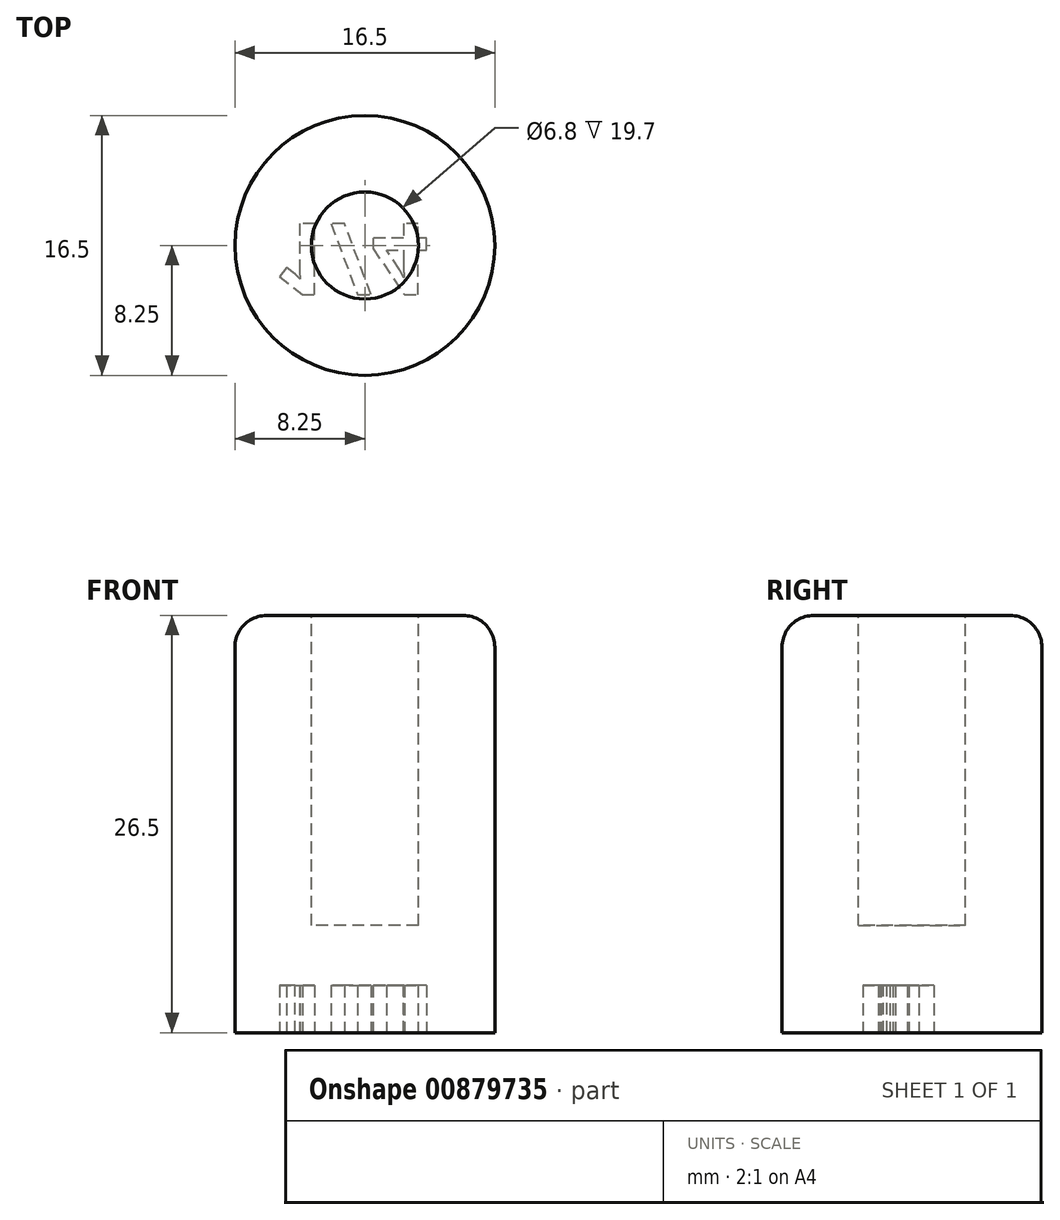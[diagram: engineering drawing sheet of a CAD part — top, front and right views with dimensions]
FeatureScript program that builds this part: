
annotation { "Feature Type Name" : "Feature", "Feature Type Description" : "" }
export const myFeature = defineFeature(function(context is Context, id is Id, definition is map)
    precondition{}
    {
        {
            var Q0;
            Q0=qCreatedBy(makeId("Top.planeOp"),FACE);
            var sketch = newSketch(context, id + "F0", { "sketchPlane" : qUnion([Q0])});
            skCircle(sketch, "E0", {"center": v(0, 0) * mm, "radius": 8.25 * mm});
            skSolve(sketch);
        }
        {
            var Q0;
            Q0=makeQuery(id+"F0.imprint","IMPRINT",FACE,{"disambiguationData":[TD([[makeQuery(id+"F0.imprint","IMPRINT",EDGE,{"derivedFrom":sQuery(id+"F0.wireOp",EDGE,"E0")}),1.0]])]});
            extrude(context, id + "F1", {"entities" : qUnion([Q0]), "depth" : 26.5 * mm, "offsetDistance" : 25 * mm});
        }
        {
            var Q0;
            Q0=makeQuery(id+"F1.opExtrude","CAP_FACE",FACE,{"disambiguationData":[OSD([sQuery(id+"F0.wireOp",EDGE,"E0")])],"isStart":false});
            cPlane(context, id + "F2", {"entities" : qUnion([Q0]), "cplaneType" : CPlaneType.OFFSET, "offset" : 0 * mm, "width" : 150 * mm, "height" : 150 * mm});
        }
        {
            var Q0;
            Q0=qCreatedBy(id+"F2.planeOp",FACE);
            var sketch = newSketch(context, id + "F3", { "sketchPlane" : qUnion([Q0])});
            skCircle(sketch, "E1", {"center": v(0, 0) * mm, "radius": 3.4 * mm});
            skSolve(sketch);
        }
        {
            var Q0;
            Q0 = qSketchRegion(id + "F3", true);
            extrude(context, id + "F4", {"entities" : qUnion([Q0]), "operationType" : NewBodyOperationType.REMOVE, "oppositeDirection" : true, "depth" : 19.7 * mm, "offsetDistance" : 25 * mm});
        }
        {
            var Q0;
            Q0=makeQuery(id+"F1.opExtrude","CAP_FACE",FACE,{"disambiguationData":[OSD([sQuery(id+"F0.wireOp",EDGE,"E0")])],"isStart":true});
            cPlane(context, id + "F5", {"entities" : qUnion([Q0]), "cplaneType" : CPlaneType.OFFSET, "offset" : 0 * mm, "width" : 150 * mm, "height" : 150 * mm});
        }
        {
            var Q0;
            Q0=qCreatedBy(id+"F5.planeOp",FACE);
            var sketch = newSketch(context, id + "F6", { "sketchPlane" : qUnion([Q0])});
            skLineSegment(sketch, "E2", {"start": v(7.64, 3.16) * mm, "end": v(-6.76, 3.16) * mm, "construction": true});
            skText(sketch, "E3", { "text": "1/4", "fontName": "OpenSans-Bold.ttf"});
            const initialGuessF6  = {"E3": [-0.0058, -0.00139, 1, 0, 0.00455]};
            skSetInitialGuess(sketch, initialGuessF6);
            skSolve(sketch);
        }
        {
            var Q0;
            Q0 = qSketchRegion(id + "F6", true);
            extrude(context, id + "F7", {"entities" : qUnion([Q0]), "operationType" : NewBodyOperationType.REMOVE, "oppositeDirection" : true, "depth" : 3 * mm, "offsetDistance" : 25 * mm});
        }
        {
            var Q0;
            Q0=makeQuery(id+"F1.opExtrude","CAP_EDGE",EDGE,{"disambiguationData":[OSD([sQuery(id+"F0.wireOp",EDGE,"E0")])],"isStart":false});
            fillet(context, id + "F8", {"entities" : qUnion([Q0]), "radius" : 2 * mm, "tangentPropagation" : true, "allowEdgeOverflow" : false});
        }
    });
